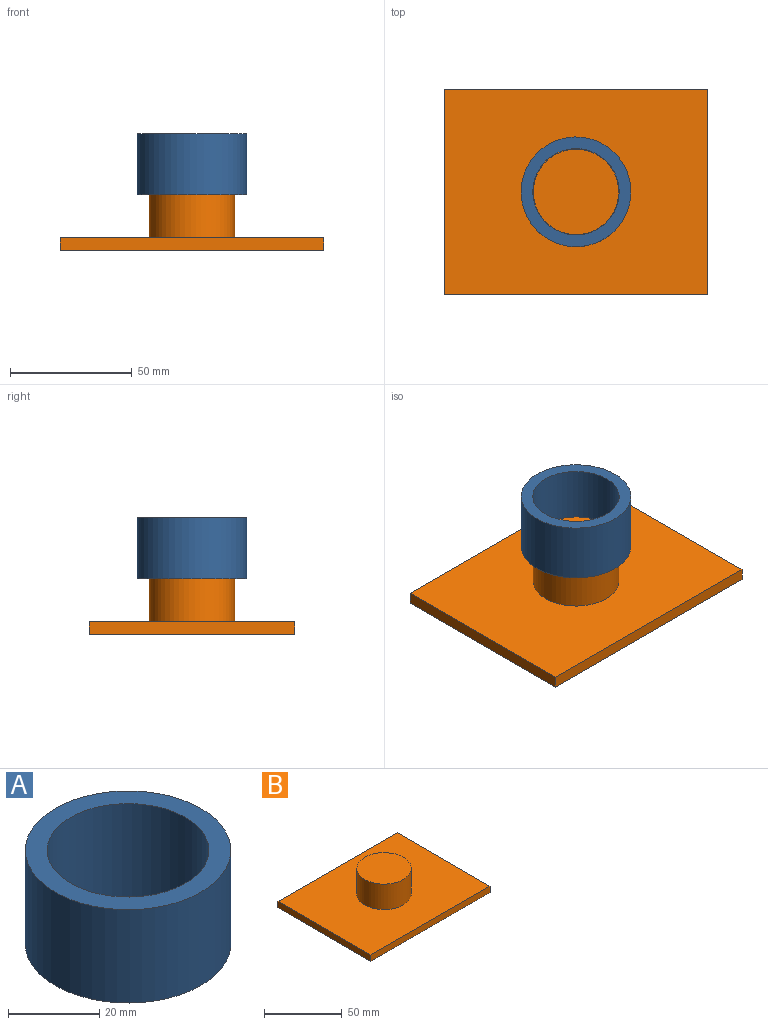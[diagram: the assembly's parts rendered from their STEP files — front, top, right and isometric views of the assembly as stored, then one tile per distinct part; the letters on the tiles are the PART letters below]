
ASSEMBLY  parts=2 mates=1
PART A: 4 faces, bbox 45x45x25 mm
  f0: cylinder r=17.7mm len=35.4mm, axis (0,0,-1), area 2780.3mm2, adj f2,f3
  f1: cylinder r=22.5mm len=45mm, axis (0,0,-1), area 3534.3mm2, adj f2,f3
  f2: plane 45x45mm, normal (0,0,1), area 606.2mm2, adj f0,f1
  f3: plane 45x45mm, normal (0,0,-1), area 606.2mm2, adj f0,f1
PART B: 8 faces, bbox 108.1x84.4x25 mm
  f0: plane 108.15x5mm, normal (0,-1,0), area 540.7mm2, adj f1,f3,f4,f5
  f1: plane 84.37x5mm, normal (1,0,0), area 421.8mm2, adj f0,f2,f4,f5
  f2: plane 108.15x5mm, normal (0,1,0), area 540.7mm2, adj f1,f3,f4,f5
  f3: plane 84.37x5mm, normal (-1,0,0), area 421.8mm2, adj f0,f2,f4,f5
  f4: plane 108.15x84.37mm, normal (0,0,1), area 8161.8mm2, adj f0,f1,f2,f3,f6
  f5: plane 108.15x84.37mm, normal (0,0,-1), area 9123.9mm2, adj f0,f1,f2,f3
  f6: cylinder r=17.5mm len=35mm, axis (0,0,-1), area 2199.1mm2, adj f4,f7
  f7: plane 35x35mm, normal (0,0,1), area 962.1mm2, adj f6
PLACE A t=(6.26,24.1,-11.6)mm
PLACE B t=(6.26,24.1,0.73)mm fixed
MATE slider B.f6 <-> A.f0  axis (0,0,1) through (6.26,24.1,25.73)mm
